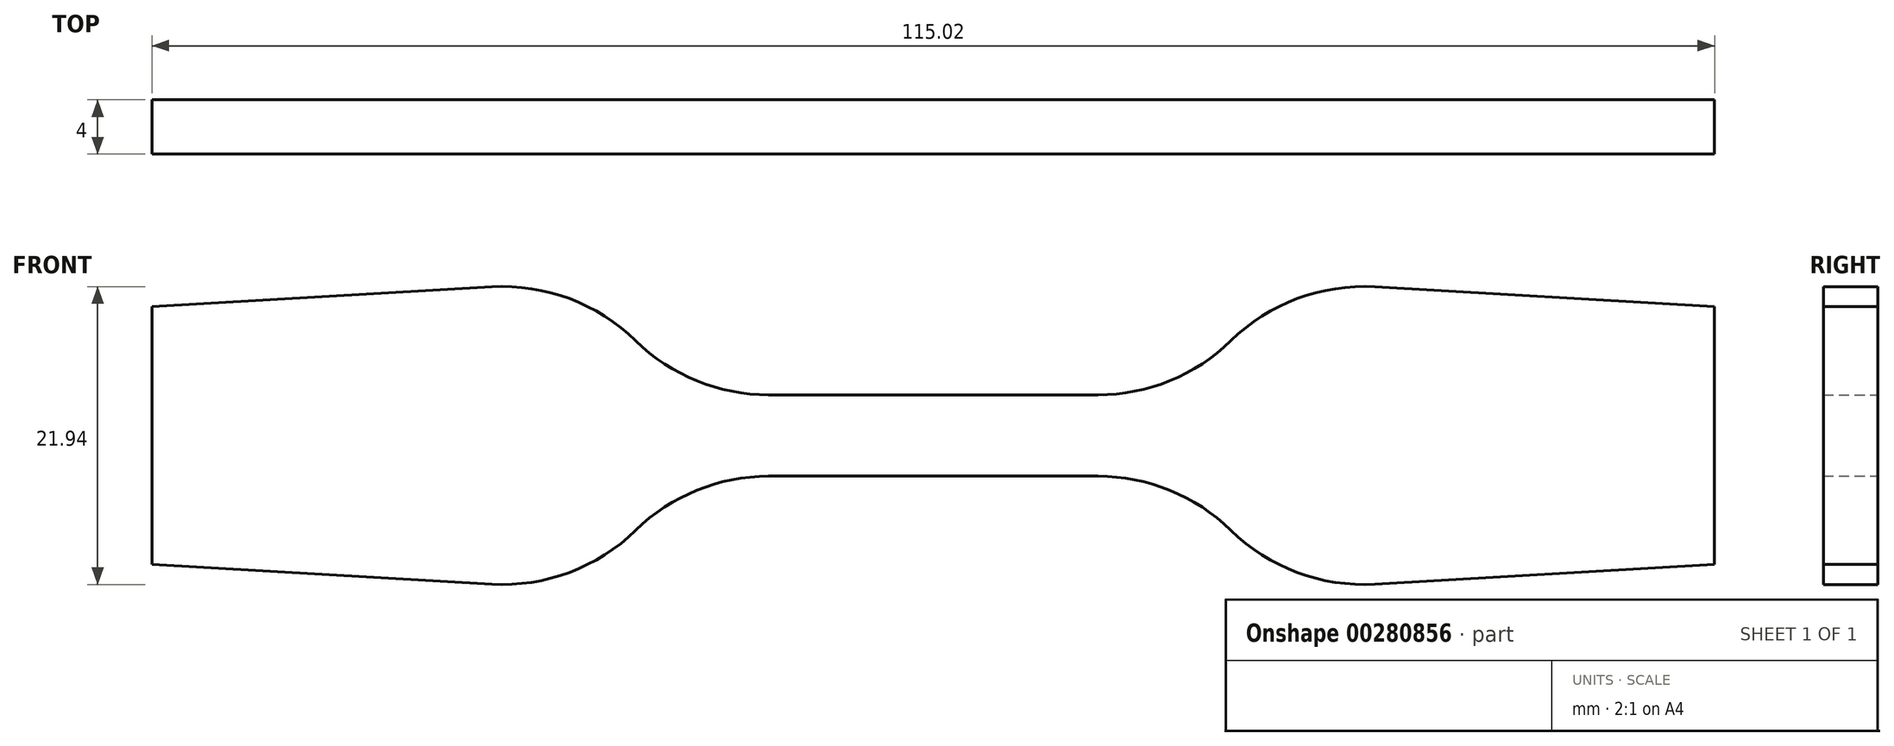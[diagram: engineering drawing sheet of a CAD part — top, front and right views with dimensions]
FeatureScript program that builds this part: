
annotation { "Feature Type Name" : "Feature", "Feature Type Description" : "" }
export const myFeature = defineFeature(function(context is Context, id is Id, definition is map)
    precondition{}
    {
        {
            var Q0;
            Q0=qCreatedBy(makeId("Front.planeOp"),FACE);
            var sketch = newSketch(context, id + "F0", { "sketchPlane" : qUnion([Q0])});
            skLineSegment(sketch, "E0", {"start": v(0, 3) * mm, "end": v(12.12, 3) * mm});
            skArc(sketch, "E1", {"start": v(32.5, 10.95) * mm, "mid": v(26.79, 10.08) * mm, "end": v(21.9, 6.98) * mm});
            skLineSegment(sketch, "E2", {"start": v(32.5, 10.95) * mm, "end": v(57.5, 9.5) * mm});
            skLineSegment(sketch, "E3", {"start": v(57.5, 9.5) * mm, "end": v(57.5, 0) * mm});
            skLineSegment(sketch, "E4.MirrorCS", {"start": v(0, -3) * mm, "end": v(12.12, -3) * mm});
            skLineSegment(sketch, "E5.MirrorCS", {"start": v(32.5, -10.95) * mm, "end": v(57.5, -9.5) * mm});
            skLineSegment(sketch, "E6.MirrorCS", {"start": v(57.5, -9.5) * mm, "end": v(57.5, 0) * mm});
            skArc(sketch, "E7.MirrorCS", {"start": v(32.5, -10.95) * mm, "mid": v(26.79, -10.08) * mm, "end": v(21.9, -6.98) * mm});
            skArc(sketch, "E8.MirrorCS", {"start": v(-32.5, -10.95) * mm, "mid": v(-26.79, -10.08) * mm, "end": v(-21.9, -6.98) * mm});
            skLineSegment(sketch, "E9.MirrorCS", {"start": v(-57.5, -9.5) * mm, "end": v(-57.5, 0) * mm});
            skArc(sketch, "E10.MirrorCS", {"start": v(-32.5, 10.95) * mm, "mid": v(-26.79, 10.08) * mm, "end": v(-21.9, 6.98) * mm});
            skLineSegment(sketch, "E11.MirrorCS", {"start": v(-32.5, 10.95) * mm, "end": v(-57.5, 9.5) * mm});
            skLineSegment(sketch, "E12.MirrorCS", {"start": v(-32.5, -10.95) * mm, "end": v(-57.5, -9.5) * mm});
            skLineSegment(sketch, "E13.MirrorCS", {"start": v(0, 3) * mm, "end": v(-12.12, 3) * mm});
            skLineSegment(sketch, "E14.MirrorCS", {"start": v(0, -3) * mm, "end": v(-12.12, -3) * mm});
            skLineSegment(sketch, "E15.MirrorCS", {"start": v(-57.5, 9.5) * mm, "end": v(-57.5, 0) * mm});
            skPoint(sketch, "E16.visualSharp", {"position": v(-19.06, 3) * mm});
            skArc(sketch, "E16.filletArc", {"start": v(-21.9, 6.98) * mm, "mid": v(-17.4, 4.03) * mm, "end": v(-12.12, 3) * mm});
            skPoint(sketch, "E17.visualSharp", {"position": v(-19.06, -3) * mm});
            skArc(sketch, "E17.filletArc", {"start": v(-12.12, -3) * mm, "mid": v(-17.4, -4.03) * mm, "end": v(-21.9, -6.98) * mm});
            skPoint(sketch, "E18.visualSharp", {"position": v(19.06, 3) * mm});
            skArc(sketch, "E18.filletArc", {"start": v(12.12, 3) * mm, "mid": v(17.4, 4.03) * mm, "end": v(21.9, 6.98) * mm});
            skPoint(sketch, "E19.visualSharp", {"position": v(19.06, -3) * mm});
            skArc(sketch, "E19.filletArc", {"start": v(21.9, -6.98) * mm, "mid": v(17.4, -4.03) * mm, "end": v(12.12, -3) * mm});
            skSolve(sketch);
        }
        {
            var Q0;
            Q0=makeQuery(id+"F0.imprint","IMPRINT",FACE,{"disambiguationData":[TD([[makeQuery(id+"F0.imprint","IMPRINT",EDGE,{"derivedFrom":sQuery(id+"F0.wireOp",EDGE,"E0")}),-1.0]])]});
            extrude(context, id + "F1", {"entities" : qUnion([Q0]), "endBound" : BoundingType.SYMMETRIC, "depth" : 4 * mm});
        }
    });
